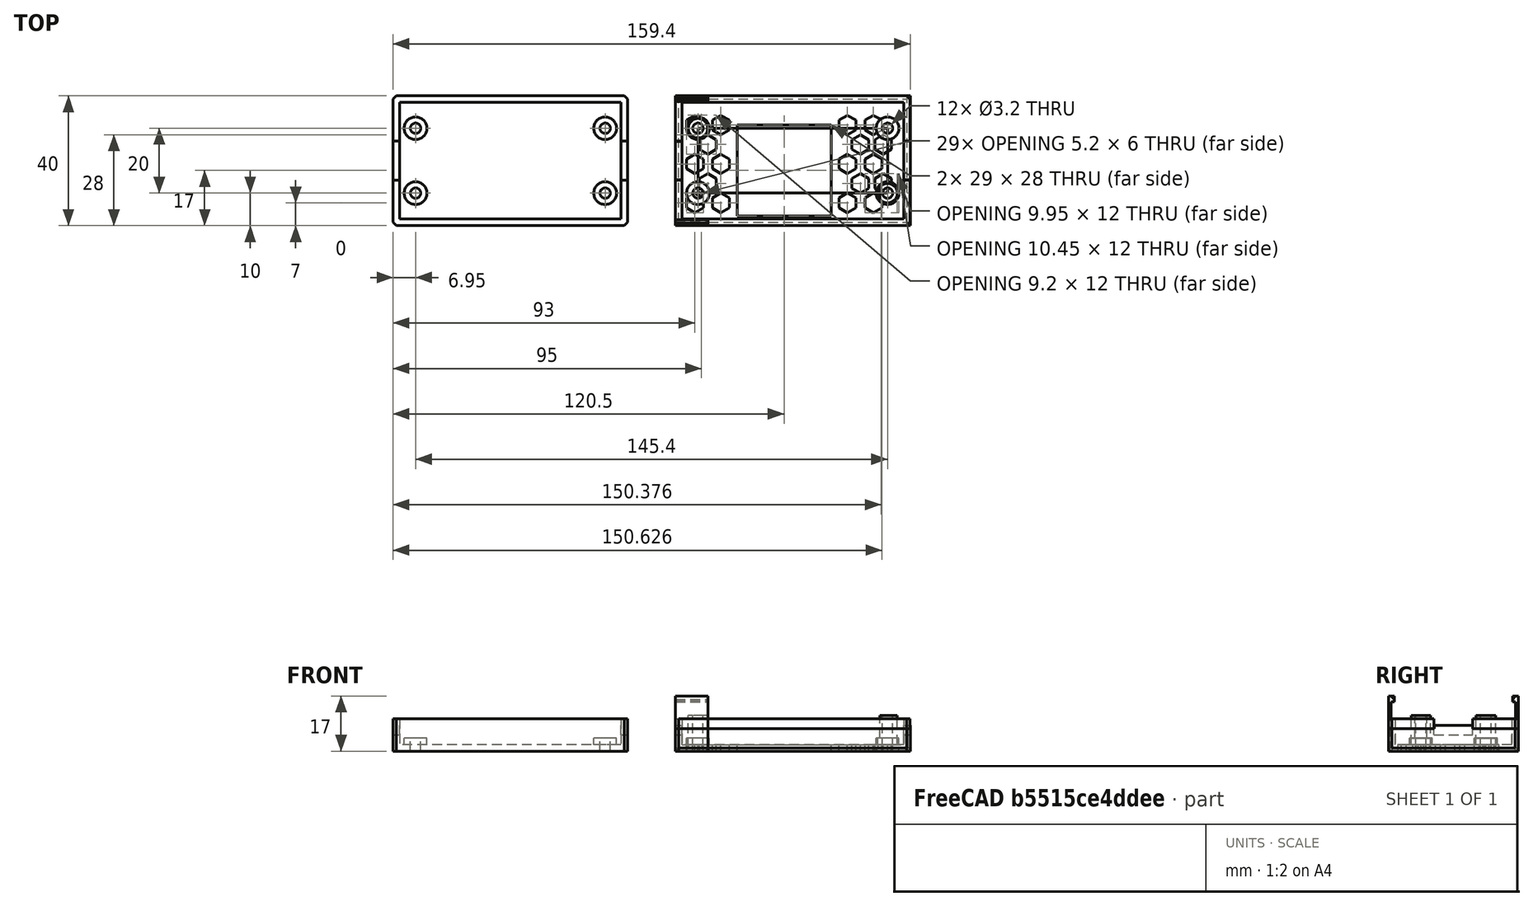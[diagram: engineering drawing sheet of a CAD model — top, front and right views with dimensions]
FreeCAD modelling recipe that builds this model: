
FCSTD DOCUMENT  (FreeCAD 0.18R14555 (Git shallow))
Label: esp32-box
License: All rights reserved
LicenseURL: http://en.wikipedia.org/wiki/All_rights_reserved
objects: Part::Box×22, Part::Feature×16, Part::MultiFuse×15, Part::Cylinder×14, Part::Cut×8, Part::Chamfer×6
note: 81 computed .brp shape members not serialized (recipe doc carries the construction recipe); baked Part::Feature solids carry a one-line shape summary decoded from their .brp

FEATURE [Part::Box] Box  label="Cube"
  AttacherType = Attacher::AttachEngine3D
  Height = 1
  Length = 67.3
  Placement = pos=(2.5,2.85,4) rot=(0,0,1;0rad)
  Width = 34.3
FEATURE [Part::Box] Box001  label="Cube001"
  AttacherType = Attacher::AttachEngine3D
  Height = 2
  Length = 58.4
  Placement = pos=(6.95,10,0) rot=(0,0,1;0rad)
  Width = 20
FEATURE [Part::Box] Box002  label="Cube002"
  AttacherType = Attacher::AttachEngine3D
  Height = 2
  Length = 72.3
  Width = 40
FEATURE [Part::Box] Box003  label="Cube003"
  AttacherType = Attacher::AttachEngine3D
  Height = 10
  Length = 2
  Width = 40
FEATURE [Part::Box] Box004  label="Cube004"
  AttacherType = Attacher::AttachEngine3D
  Height = 10
  Length = 2
  Placement = pos=(70.3,0,0) rot=(0,0,1;0rad)
  Width = 40
FEATURE [Part::Box] Box005  label="Cube005"
  AttacherType = Attacher::AttachEngine3D
  Height = 10
  Length = 72.3
  Width = 2
FEATURE [Part::Box] Box006  label="Cube006"
  AttacherType = Attacher::AttachEngine3D
  Height = 10
  Length = 72.3
  Placement = pos=(0,38,0) rot=(0,0,1;0rad)
  Width = 2
FEATURE [Part::MultiFuse] Fusion  label="wall"
  Shapes = -> [Box006,Box005,Box004,Box003]
FEATURE [Part::Cylinder] Cylinder
  Angle = 360
  AttacherType = Attacher::AttachEngine3D
  Height = 5
  Placement = pos=(6.95,10,0) rot=(0,0,1;0rad)
  Radius = 3.5
FEATURE [Part::Cylinder] Cylinder001
  Angle = 360
  AttacherType = Attacher::AttachEngine3D
  Height = 5
  Placement = pos=(65.35,10,0) rot=(0,0,1;0rad)
  Radius = 3.5
FEATURE [Part::Cylinder] Cylinder002
  Angle = 360
  AttacherType = Attacher::AttachEngine3D
  Height = 5
  Placement = pos=(65.35,30,0) rot=(0,0,1;0rad)
  Radius = 3.5
FEATURE [Part::Cylinder] Cylinder003
  Angle = 360
  AttacherType = Attacher::AttachEngine3D
  Height = 5
  Placement = pos=(6.95,30,0) rot=(0,0,1;0rad)
  Radius = 3.5
FEATURE [Part::Cylinder] Cylinder004
  Angle = 360
  AttacherType = Attacher::AttachEngine3D
  Height = 5
  Placement = pos=(6.95,30,0) rot=(0,0,1;0rad)
  Radius = 1.6
FEATURE [Part::Cylinder] Cylinder005
  Angle = 360
  AttacherType = Attacher::AttachEngine3D
  Height = 5
  Placement = pos=(65.35,30,0) rot=(0,0,1;0rad)
  Radius = 1.6
FEATURE [Part::Cylinder] Cylinder006
  Angle = 360
  AttacherType = Attacher::AttachEngine3D
  Height = 5
  Placement = pos=(65.35,10,0) rot=(0,0,1;0rad)
  Radius = 1.6
FEATURE [Part::Cylinder] Cylinder007
  Angle = 360
  AttacherType = Attacher::AttachEngine3D
  Height = 5
  Placement = pos=(6.95,10,0) rot=(0,0,1;0rad)
  Radius = 1.6
FEATURE [Part::MultiFuse] Fusion001
  Shapes = -> [Cylinder003,Cylinder002,Cylinder001,Cylinder]
FEATURE [Part::MultiFuse] Fusion002
  Shapes = -> [Cylinder007,Cylinder006,Cylinder004,Cylinder005]
FEATURE [Part::MultiFuse] Fusion003
  Shapes = -> [Box002,Fusion]
FEATURE [Part::MultiFuse] Fusion004
  Shapes = -> [Fusion001,Fusion003]
FEATURE [Part::Cut] Cut
  Base = -> Fusion004
  Tool = -> Fusion002
FEATURE [Part::Box] Box007  label="Cube007"
  AttacherType = Attacher::AttachEngine3D
  Height = 5
  Length = 2
  Placement = pos=(0,14,2) rot=(0,0,1;0rad)
  Width = 12
FEATURE [Part::Box] Box008  label="Cube008"
  AttacherType = Attacher::AttachEngine3D
  Height = 5
  Length = 2
  Placement = pos=(70.3,14,2) rot=(0,0,1;0rad)
  Width = 12
FEATURE [Part::MultiFuse] Fusion005
  Placement = pos=(0,0,3) rot=(0,0,1;0rad)
  Shapes = -> [Box008,Box007]
FEATURE [Part::Cut] Cut001
  Base = -> Cut
  Tool = -> Fusion005
FEATURE [Part::Cut] Cut002
  Base = -> Cut001
  Tool = -> Box
FEATURE [Part::Box] Box013  label="Cube013"
  AttacherType = Attacher::AttachEngine3D
  Height = 2
  Length = 72.4
  Width = 40
FEATURE [Part::Box] Box014  label="Cube014"
  AttacherType = Attacher::AttachEngine3D
  Height = 7
  Length = 72.4
  Width = 2
FEATURE [Part::Box] Box015  label="Cube015"
  AttacherType = Attacher::AttachEngine3D
  Height = 7
  Length = 72.4
  Placement = pos=(0,38,0) rot=(0,0,1;0rad)
  Width = 2
FEATURE [Part::Box] Box016  label="Cube016"
  AttacherType = Attacher::AttachEngine3D
  Height = 7
  Length = 2
  Width = 40
FEATURE [Part::Box] Box017  label="Cube017"
  AttacherType = Attacher::AttachEngine3D
  Height = 7
  Length = 2
  Placement = pos=(70.4,0,0) rot=(0,0,1;0rad)
  Width = 40
FEATURE [Part::Box] Box018  label="Cube018"
  AttacherType = Attacher::AttachEngine3D
  Height = 1
  Length = 2
  Placement = pos=(70.4,14.1,7) rot=(0,0,1;0rad)
  Width = 11.9
FEATURE [Part::Box] Box019  label="Cube019"
  AttacherType = Attacher::AttachEngine3D
  Height = 1
  Length = 2
  Placement = pos=(0,14.1,7) rot=(0,0,1;0rad)
  Width = 11.8
FEATURE [Part::Box] Box020  label="Cube020"
  AttacherType = Attacher::AttachEngine3D
  Height = 17
  Length = 10
  Placement = pos=(0,39.2,0) rot=(0,0,1;0rad)
  Width = 0.8
FEATURE [Part::Box] Box021  label="Cube021"
  AttacherType = Attacher::AttachEngine3D
  Height = 1.8
  Length = 10
  Placement = pos=(0,38.2,15.2) rot=(0,0,1;0rad)
  Width = 1.8
FEATURE [Part::Box] Box022  label="Cube022"
  AttacherType = Attacher::AttachEngine3D
  Height = 1.8
  Length = 10
  Placement = pos=(0,0,15.2) rot=(0,0,1;0rad)
  Width = 1.8
FEATURE [Part::Box] Box023  label="Cube023"
  AttacherType = Attacher::AttachEngine3D
  Height = 17
  Length = 10
  Width = 0.8
FEATURE [Part::MultiFuse] Fusion006002003
  Shapes = -> [Box020,Box021]
FEATURE [Part::MultiFuse] Fusion006002004
  Shapes = -> [Box023,Box022]
FEATURE [Part::Feature] Fusion006002004001  label="Fusion006002005"
  shape: bbox 10 x 1.8 x 17 mm, 8 faces (baked)
FEATURE [Part::Feature] Fusion006002003001  label="Fusion006002006"
  shape: bbox 10 x 1.8 x 17 mm, 8 faces (baked)
FEATURE [Part::Chamfer] Chamfer002
  Base = -> Fusion006002003001
  Edges = 1 edges r=1: [Edge12]
FEATURE [Part::Chamfer] Chamfer003
  Base = -> Fusion006002004001
  Edges = 1 edges r=1: [Edge12]
FEATURE [Part::Chamfer] Chamfer004
  Base = -> Chamfer002
  Edges = 1 edges r=0.5: [Edge3]
FEATURE [Part::Chamfer] Chamfer005
  Base = -> Chamfer003
  Edges = 1 edges r=0.5: [Edge3]
FEATURE [Part::Box] Box024  label="Cube024"
  AttacherType = Attacher::AttachEngine3D
  Height = 2
  Length = 29
  Placement = pos=(19,3,0) rot=(0,0,1;0rad)
  Width = 28
FEATURE [Part::Feature] Body001
  Placement = pos=(27,-6,0) rot=(0,0,1;0rad)
  shape: bbox 5.196 x 6 x 2 mm, 8 faces (baked)
FEATURE [Part::Feature] Body002
  Placement = pos=(23,0,0) rot=(0,0,1;0rad)
  shape: bbox 5.196 x 6 x 2 mm, 8 faces (baked)
FEATURE [Part::Feature] Body003
  Placement = pos=(27,6,0) rot=(0,0,1;0rad)
  shape: bbox 5.196 x 6 x 2 mm, 8 faces (baked)
FEATURE [Part::Feature] Body004
  Placement = pos=(23,12,0) rot=(0,0,1;0rad)
  shape: bbox 5.196 x 6 x 2 mm, 8 faces (baked)
FEATURE [Part::Feature] Body005
  Placement = pos=(27,18,0) rot=(0,0,1;0rad)
  shape: bbox 5.196 x 6 x 2 mm, 8 faces (baked)
FEATURE [Part::Feature] Body006
  Placement = pos=(19,-6,0) rot=(0,0,1;0rad)
  shape: bbox 5.196 x 6 x 2 mm, 8 faces (baked)
FEATURE [Part::Feature] Body007
  Placement = pos=(19,6,0) rot=(0,0,1;0rad)
  shape: bbox 5.196 x 6 x 2 mm, 8 faces (baked)
FEATURE [Part::Feature] Body008
  Placement = pos=(19,18,0) rot=(0,0,1;0rad)
  shape: bbox 5.196 x 6 x 2 mm, 8 faces (baked)
FEATURE [Part::MultiFuse] Fusion006002004003
  Placement = pos=(-1,1,0) rot=(0,0,1;0rad)
  Shapes = -> [Body001,Body005,Body008,Body003,Body002,Body006,Body004,Body007]
FEATURE [Part::Feature] Fusion006002004003001  label="Fusion006002004004"
  Placement = pos=(46,1,0) rot=(0,0,1;0rad)
  shape: bbox 13.2 x 30 x 2 mm, 64 faces, 8 solids (baked)
FEATURE [Part::Feature] Body013
  Placement = pos=(76,1,0) rot=(0,0,1;0rad)
  shape: bbox 5.196 x 6 x 2 mm, 8 faces (baked)
FEATURE [Part::Feature] Body015
  Placement = pos=(76,13,0) rot=(0,0,1;0rad)
  shape: bbox 5.196 x 6 x 2 mm, 8 faces (baked)
FEATURE [Part::MultiFuse] Fusion006002004003002
  Shapes = -> [Body015,Body013,Fusion006002004003001]
FEATURE [Part::MultiFuse] Fusion006002004003003
  Shapes = -> [Fusion006002004003,Fusion006002004003002]
FEATURE [Part::MultiFuse] Fusion006002004003004
  Shapes = -> [Box019,Box018,Box017,Box016,Box015,Box014,Box013]
FEATURE [Part::Cut] Cut004
  Base = -> Fusion006002004003004
  Tool = -> Box024
FEATURE [Part::Cut] Cut005
  Base = -> Cut004
  Tool = -> Fusion006002004003003
FEATURE [Part::Cylinder] Cylinder008
  Angle = 360
  AttacherType = Attacher::AttachEngine3D
  Height = 11
  Placement = pos=(6.95,30,0) rot=(0,0,1;0rad)
  Radius = 3
FEATURE [Part::Cylinder] Cylinder009
  Angle = 360
  AttacherType = Attacher::AttachEngine3D
  Height = 11
  Placement = pos=(65.35,10,0) rot=(0,0,1;0rad)
  Radius = 3
FEATURE [Part::Cylinder] Cylinder010
  Angle = 360
  AttacherType = Attacher::AttachEngine3D
  Height = 11
  Placement = pos=(65.35,10,0) rot=(0,0,1;0rad)
  Radius = 1.6
FEATURE [Part::Cylinder] Cylinder011
  Angle = 360
  AttacherType = Attacher::AttachEngine3D
  Height = 11
  Placement = pos=(6.95,30,0) rot=(0,0,1;0rad)
  Radius = 1.6
FEATURE [Part::MultiFuse] Fusion006002004003005
  Shapes = -> [Cut005,Cylinder008,Cylinder009]
FEATURE [Part::MultiFuse] Fusion006002004003006
  Shapes = -> [Cylinder011,Cylinder010]
FEATURE [Part::Cut] Cut006
  Base = -> Fusion006002004003005
  Tool = -> Fusion006002004003006
FEATURE [Part::Box] Box025  label="Cube025"
  AttacherType = Attacher::AttachEngine3D
  Height = 7
  Length = 10
  Placement = pos=(53,5,4) rot=(0,0,1;0rad)
  Width = 10
FEATURE [Part::Cut] Cut007
  Base = -> Cut006
  Tool = -> Box025
FEATURE [Part::Cylinder] Cylinder012
  Angle = 360
  AttacherType = Attacher::AttachEngine3D
  Height = 1
  Placement = pos=(65.35,10,0) rot=(0,0,1;0rad)
  Radius = 3.5
FEATURE [Part::Cylinder] Cylinder013
  Angle = 360
  AttacherType = Attacher::AttachEngine3D
  Height = 1
  Placement = pos=(6.95,30,0) rot=(0,0,1;0rad)
  Radius = 3.5
FEATURE [Part::MultiFuse] Fusion006002004003007
  Shapes = -> [Cylinder013,Cylinder012]
FEATURE [Part::Cut] Cut008
  Base = -> Cut007
  Tool = -> Fusion006002004003007
FEATURE [Part::Feature] Cut008001  label="Cut009"
  shape: bbox 72.4 x 40 x 11 mm, 141 faces (baked)
FEATURE [Part::Chamfer] Chamfer006
  Base = -> Cut008001
  Edges = 8 edges r=1: [Edge413,Edge414,Edge415,Edge416,Edge427,Edge428,Edge429,Edge430]
FEATURE [Part::Chamfer] Chamfer
  Base = -> Cut002
  Edges = 8 edges r=1: [Edge101,Edge103,Edge110,Edge120,Edge133,Edge135,Edge139,Edge143]
FEATURE [Part::Feature] Chamfer007
  Placement = pos=(-87,0,0) rot=(0,0,1;0rad)
  shape: bbox 72.3 x 40 x 10 mm, 34 faces (baked)
FEATURE [Part::Feature] Chamfer006001  label="Chamfer008"
  shape: bbox 72.4 x 40 x 11 mm, 153 faces (baked)
